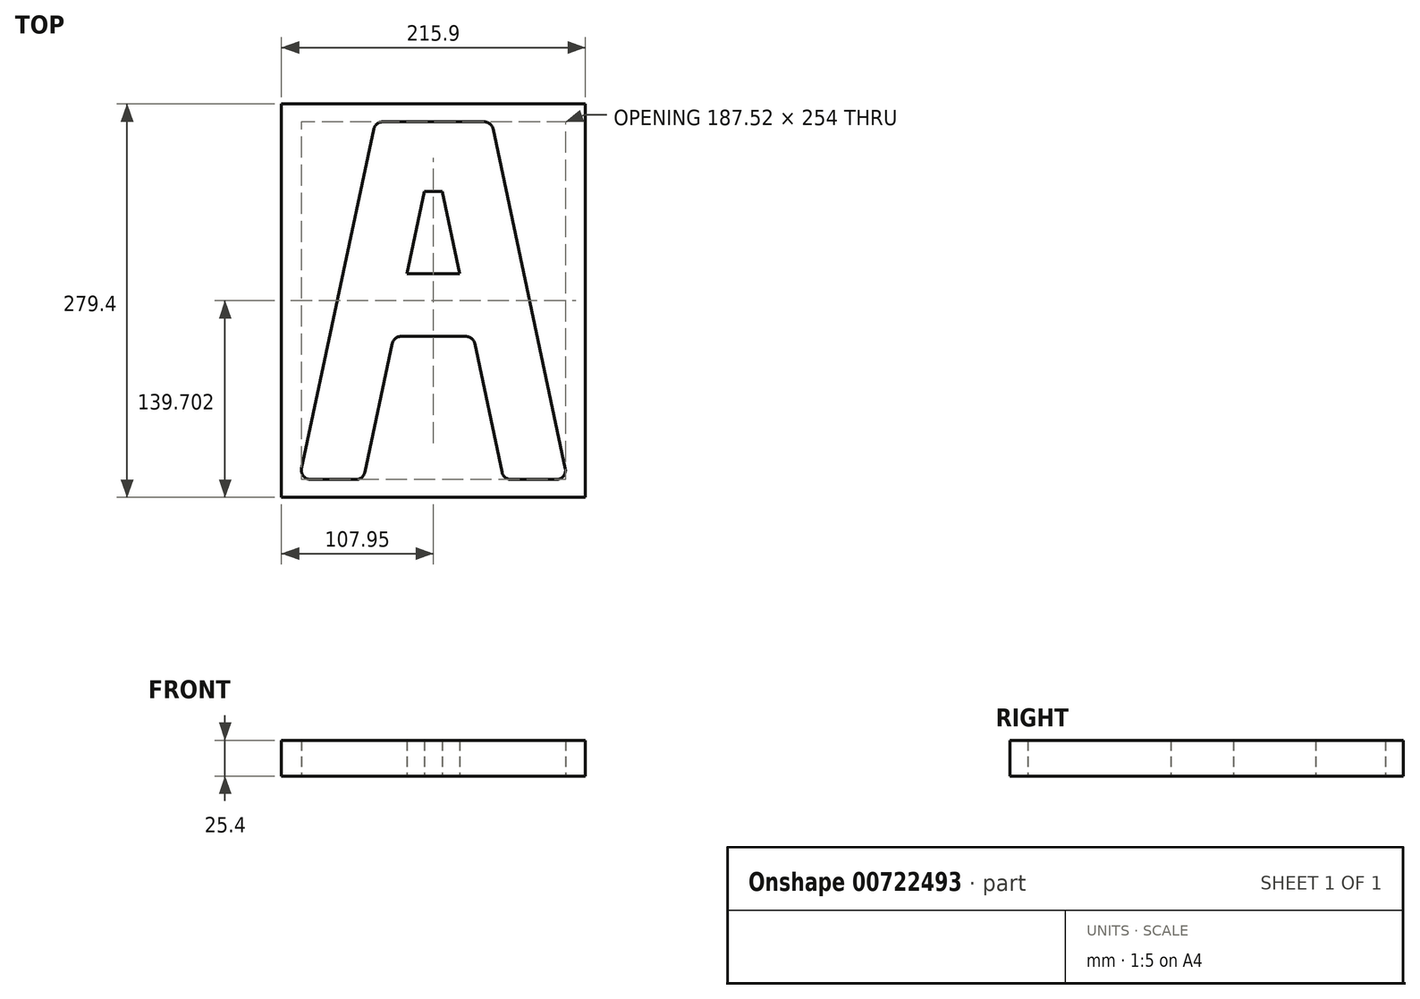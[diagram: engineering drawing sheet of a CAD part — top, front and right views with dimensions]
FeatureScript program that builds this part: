
annotation { "Feature Type Name" : "Feature", "Feature Type Description" : "" }
export const myFeature = defineFeature(function(context is Context, id is Id, definition is map)
    precondition{}
    {
        {
            var Q0;
            Q0=qCreatedBy(makeId("Top.planeOp"),FACE);
            var sketch = newSketch(context, id + "F0", { "sketchPlane" : qUnion([Q0])});
            skLineSegment(sketch, "E0.bottom", {"start": v(-107.95, 153.84) * mm, "end": v(107.95, 153.84) * mm});
            skLineSegment(sketch, "E0.top", {"start": v(-107.95, -125.56) * mm, "end": v(107.95, -125.56) * mm});
            skLineSegment(sketch, "E0.left", {"start": v(-107.95, 153.84) * mm, "end": v(-107.95, -125.56) * mm});
            skLineSegment(sketch, "E0.right", {"start": v(107.95, 153.84) * mm, "end": v(107.95, -125.56) * mm});
            skLineSegment(sketch, "E1", {"start": v(-42.33, 136.11) * mm, "end": v(-93.62, -105.19) * mm});
            skLineSegment(sketch, "E2", {"start": v(-87.4, -112.86) * mm, "end": v(-54.95, -112.86) * mm});
            skLineSegment(sketch, "E3", {"start": v(-48.74, -107.83) * mm, "end": v(-29.28, -16.29) * mm});
            skLineSegment(sketch, "E4", {"start": v(0, 153.84) * mm, "end": v(0, -125.56) * mm, "construction": true});
            skLineSegment(sketch, "E5", {"start": v(-36.12, 141.14) * mm, "end": v(0, 141.14) * mm});
            skLineSegment(sketch, "E6", {"start": v(-23.07, -11.26) * mm, "end": v(0, -11.26) * mm});
            skLineSegment(sketch, "E7", {"start": v(0, 96.7) * mm, "end": v(-0.12, 96.7) * mm});
            skLineSegment(sketch, "E8", {"start": v(-6.33, 91.66) * mm, "end": v(-17.13, 40.86) * mm});
            skLineSegment(sketch, "E9", {"start": v(-10.92, 33.2) * mm, "end": v(0, 33.2) * mm});
            skPoint(sketch, "E10.visualSharp", {"position": v(-41.26, 141.14) * mm});
            skArc(sketch, "E10.filletArc", {"start": v(-36.12, 141.14) * mm, "mid": v(-40.11, 139.73) * mm, "end": v(-42.33, 136.11) * mm});
            skPoint(sketch, "E11.visualSharp", {"position": v(-95.25, -112.86) * mm});
            skArc(sketch, "E11.filletArc", {"start": v(-93.62, -105.19) * mm, "mid": v(-92.34, -110.5) * mm, "end": v(-87.4, -112.86) * mm});
            skPoint(sketch, "E12.visualSharp", {"position": v(-49.8, -112.86) * mm});
            skArc(sketch, "E12.filletArc", {"start": v(-54.95, -112.86) * mm, "mid": v(-50.95, -111.44) * mm, "end": v(-48.74, -107.83) * mm});
            skPoint(sketch, "E13.visualSharp", {"position": v(-28.21, -11.26) * mm});
            skArc(sketch, "E13.filletArc", {"start": v(-23.07, -11.26) * mm, "mid": v(-27.07, -12.67) * mm, "end": v(-29.28, -16.29) * mm});
            skPoint(sketch, "E14.visualSharp", {"position": v(-18.76, 33.2) * mm});
            skLineSegment(sketch, "E15.MirrorCS", {"start": v(23.07, -11.26) * mm, "end": v(0, -11.26) * mm});
            skLineSegment(sketch, "E16.MirrorCS", {"start": v(48.74, -107.83) * mm, "end": v(29.28, -16.29) * mm});
            skLineSegment(sketch, "E17.MirrorCS", {"start": v(42.33, 136.11) * mm, "end": v(93.62, -105.19) * mm});
            skLineSegment(sketch, "E18.MirrorCS", {"start": v(87.4, -112.86) * mm, "end": v(54.95, -112.86) * mm});
            skLineSegment(sketch, "E19.MirrorCS", {"start": v(6.33, 91.66) * mm, "end": v(17.13, 40.86) * mm});
            skLineSegment(sketch, "E20.MirrorCS", {"start": v(10.92, 33.2) * mm, "end": v(0, 33.2) * mm});
            skPoint(sketch, "E21.MirrorP", {"position": v(18.76, 33.2) * mm});
            skArc(sketch, "E22.MirrorCS", {"start": v(23.07, -11.26) * mm, "mid": v(27.07, -12.67) * mm, "end": v(29.28, -16.29) * mm});
            skArc(sketch, "E23.MirrorCS", {"start": v(54.95, -112.86) * mm, "mid": v(50.95, -111.44) * mm, "end": v(48.74, -107.83) * mm});
            skArc(sketch, "E24.MirrorCS", {"start": v(93.62, -105.19) * mm, "mid": v(92.34, -110.5) * mm, "end": v(87.4, -112.86) * mm});
            skLineSegment(sketch, "E25.MirrorCS", {"start": v(36.12, 141.14) * mm, "end": v(0, 141.14) * mm});
            skArc(sketch, "E26.MirrorCS", {"start": v(36.12, 141.14) * mm, "mid": v(40.11, 139.73) * mm, "end": v(42.33, 136.11) * mm});
            skLineSegment(sketch, "E27", {"start": v(-17.13, 40.86) * mm, "end": v(-18.76, 33.2) * mm});
            skLineSegment(sketch, "E28", {"start": v(-10.92, 33.2) * mm, "end": v(18.76, 33.2) * mm});
            skLineSegment(sketch, "E29", {"start": v(17.13, 40.86) * mm, "end": v(18.76, 33.2) * mm});
            skPoint(sketch, "E30.orphan", {"position": v(-6.33, 91.66) * mm});
            skPoint(sketch, "E31.orphan", {"position": v(6.33, 91.66) * mm});
            skLineSegment(sketch, "E32", {"start": v(-6.33, 91.66) * mm, "end": v(6.33, 91.66) * mm});
            skLineSegment(sketch, "E33", {"start": v(-10.92, 33.2) * mm, "end": v(-18.76, 33.2) * mm});
            skSolve(sketch);
        }
        {
            var Q0;
            Q0=makeQuery(id+"F0.imprint","IMPRINT",FACE,{"disambiguationData":[TD([[makeQuery(id+"F0.imprint","IMPRINT",EDGE,{"derivedFrom":sQuery(id+"F0.wireOp",EDGE,"E8")}),1.0]])]});
            var Q1;
            Q1=makeQuery(id+"F0.imprint","IMPRINT",FACE,{"disambiguationData":[TD([[makeQuery(id+"F0.imprint","IMPRINT",EDGE,{"derivedFrom":sQuery(id+"F0.wireOp",EDGE,"E0.bottom")}),-1.0]])]});
            extrude(context, id + "F1", {"entities" : qUnion([Q0, Q1]), "depth" : 25.4 * mm, "offsetDistance" : 25.4 * mm});
        }
    });
